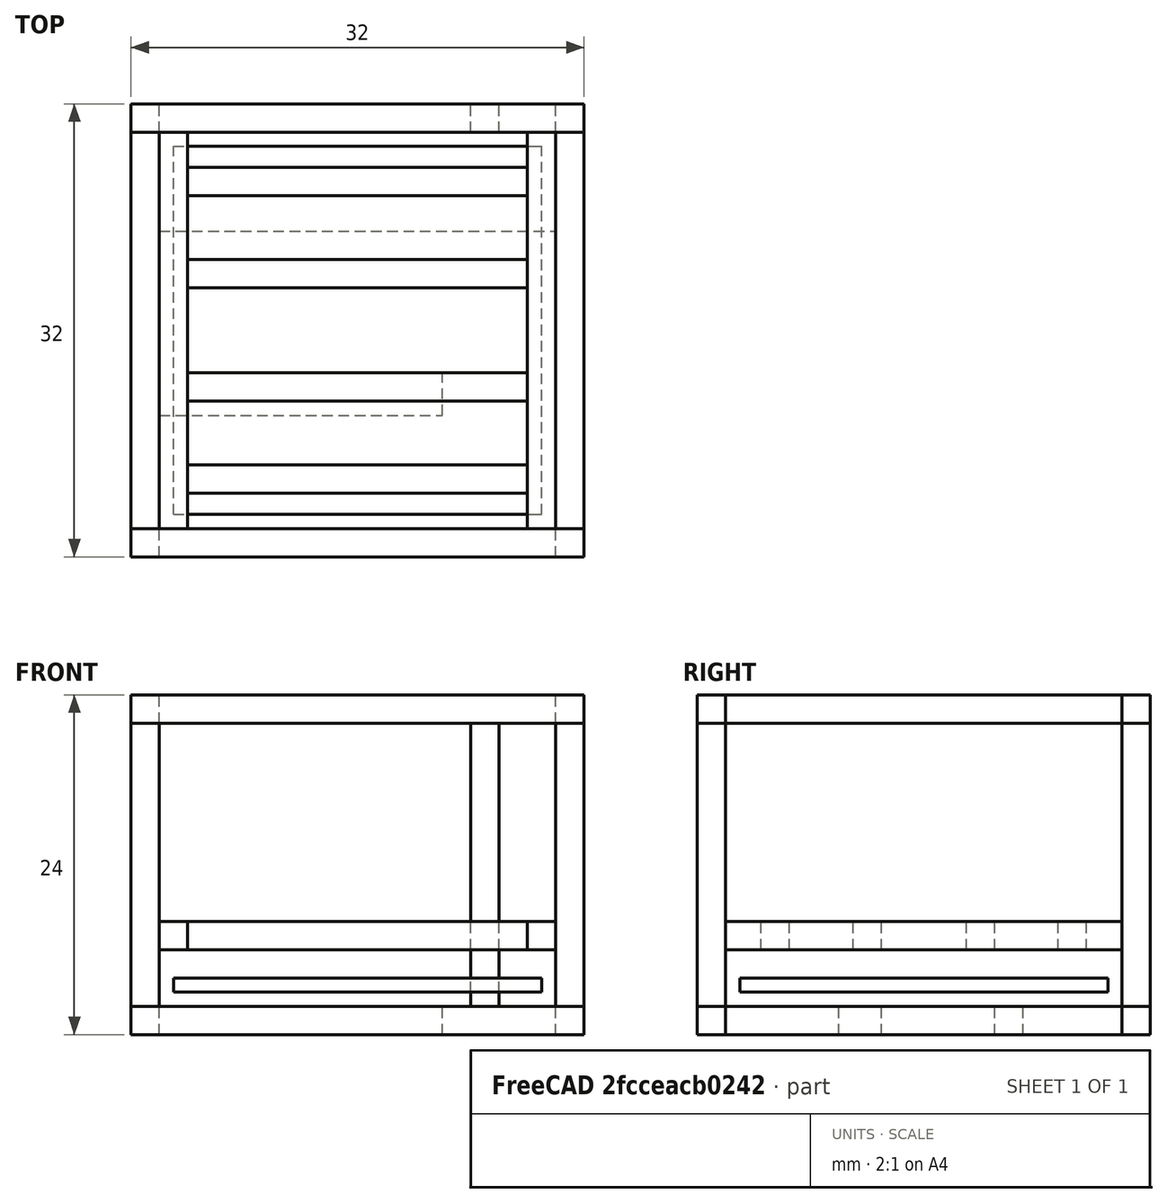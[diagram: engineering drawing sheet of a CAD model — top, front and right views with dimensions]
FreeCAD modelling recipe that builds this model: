
FCSTD DOCUMENT  (FreeCAD 0.18R14555 (Git shallow))
Label: filament-dryer
License: All rights reserved
LicenseURL: http://en.wikipedia.org/wiki/All_rights_reserved
objects: Part::Box×22
note: 22 computed .brp shape members not serialized (recipe doc carries the construction recipe); baked Part::Feature solids carry a one-line shape summary decoded from their .brp

FEATURE [Part::Box] Box  label="32L-000"
  AttacherType = Attacher::AttachEngine3D
  Height = 2
  Length = 32
  Width = 2
FEATURE [Part::Box] Box001  label="32L-001"
  AttacherType = Attacher::AttachEngine3D
  Height = 2
  Length = 32
  Placement = pos=(0,0,22) rot=(0,0,1;0rad)
  Width = 2
FEATURE [Part::Box] Box002  label="20L-000"
  AttacherType = Attacher::AttachEngine3D
  Height = 20
  Length = 2
  Placement = pos=(0,0,2) rot=(0,0,1;0rad)
  Width = 2
FEATURE [Part::Box] Box003  label="20L-001"
  AttacherType = Attacher::AttachEngine3D
  Height = 20
  Length = 2
  Placement = pos=(30,0,2) rot=(0,0,1;0rad)
  Width = 2
FEATURE [Part::Box] Box004  label="28L-000"
  AttacherType = Attacher::AttachEngine3D
  Height = 2
  Length = 2
  Placement = pos=(0,2,0) rot=(0,0,1;0rad)
  Width = 28
FEATURE [Part::Box] Box005  label="28L-001"
  AttacherType = Attacher::AttachEngine3D
  Height = 2
  Length = 2
  Placement = pos=(30,2,0) rot=(0,0,1;0rad)
  Width = 28
FEATURE [Part::Box] Box006  label="28L-002"
  AttacherType = Attacher::AttachEngine3D
  Height = 2
  Length = 2
  Placement = pos=(30,2,22) rot=(0,0,1;0rad)
  Width = 28
FEATURE [Part::Box] Box007  label="28L-003"
  AttacherType = Attacher::AttachEngine3D
  Height = 2
  Length = 2
  Placement = pos=(0,2,22) rot=(0,0,1;0rad)
  Width = 28
FEATURE [Part::Box] Box008  label="32L-002"
  AttacherType = Attacher::AttachEngine3D
  Height = 2
  Length = 32
  Placement = pos=(0,30,0) rot=(0,0,1;0rad)
  Width = 2
FEATURE [Part::Box] Box009  label="32L-003"
  AttacherType = Attacher::AttachEngine3D
  Height = 2
  Length = 32
  Placement = pos=(0,30,22) rot=(0,0,1;0rad)
  Width = 2
FEATURE [Part::Box] Box010  label="20L-002"
  AttacherType = Attacher::AttachEngine3D
  Height = 20
  Length = 2
  Placement = pos=(0,30,2) rot=(0,0,1;0rad)
  Width = 2
FEATURE [Part::Box] Box011  label="20L-003"
  AttacherType = Attacher::AttachEngine3D
  Height = 20
  Length = 2
  Placement = pos=(30,30,2) rot=(0,0,1;0rad)
  Width = 2
FEATURE [Part::Box] Box012  label="28L-004"
  AttacherType = Attacher::AttachEngine3D
  Height = 2
  Length = 20
  Placement = pos=(2,10,0) rot=(0,0,1;0rad)
  Width = 3
FEATURE [Part::Box] Box013  label="28L-005"
  AttacherType = Attacher::AttachEngine3D
  Height = 2
  Length = 28
  Placement = pos=(2,21,0) rot=(0,0,1;0rad)
  Width = 2
FEATURE [Part::Box] Box014  label="Heated-bed"
  AttacherType = Attacher::AttachEngine3D
  Height = 1
  Length = 26
  Placement = pos=(3,3,3) rot=(0,0,1;0rad)
  Width = 26
FEATURE [Part::Box] Box015  label="20L-004"
  AttacherType = Attacher::AttachEngine3D
  Height = 20
  Length = 2
  Placement = pos=(24,30,2) rot=(0,0,1;0rad)
  Width = 2
FEATURE [Part::Box] Box016  label="28L-006"
  AttacherType = Attacher::AttachEngine3D
  Height = 2
  Length = 2
  Placement = pos=(2,2,6) rot=(0,0,1;0rad)
  Width = 28
FEATURE [Part::Box] Box017  label="28L-007"
  AttacherType = Attacher::AttachEngine3D
  Height = 2
  Length = 2
  Placement = pos=(28,2,6) rot=(0,0,1;0rad)
  Width = 28
FEATURE [Part::Box] Box018  label="24L-000"
  AttacherType = Attacher::AttachEngine3D
  Height = 2
  Length = 24
  Placement = pos=(4,4.5,6) rot=(0,0,1;0rad)
  Width = 2
FEATURE [Part::Box] Box019  label="24L-001"
  AttacherType = Attacher::AttachEngine3D
  Height = 2
  Length = 24
  Placement = pos=(4,25.5,6) rot=(0,0,1;0rad)
  Width = 2
FEATURE [Part::Box] Box020  label="24L-002"
  AttacherType = Attacher::AttachEngine3D
  Height = 2
  Length = 24
  Placement = pos=(4,19,6) rot=(0,0,1;0rad)
  Width = 2
FEATURE [Part::Box] Box021  label="24L-003"
  AttacherType = Attacher::AttachEngine3D
  Height = 2
  Length = 24
  Placement = pos=(4,11,6) rot=(0,0,1;0rad)
  Width = 2
